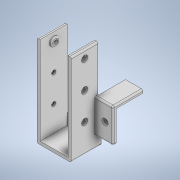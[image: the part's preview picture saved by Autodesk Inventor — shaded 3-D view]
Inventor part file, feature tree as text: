
AUTODESK INVENTOR PART (.ipt)
format: ipt  version: 2020 (Build 240168000, 168)  size: 286,208 bytes
history: native  units: in
note: dims shown in document units (in); Inventor stores cm internally (conversion verified against a paired STEP export)
features: extrude x12, sketch x12, fillet x3, mirror x2, pattern_linear x1
ambient origin geometry x8: Origin, YZ Plane, XZ Plane, XY Plane, X Axis, Y Axis, Z Axis, Center Point
bodies: Solid1 (feature_tree)
feature tree (30):
  extrude  "Extrusion1"  Depth=1.0in
  extrude  "Extrusion2"  Depth=0.1181in
  extrude  "Extrusion3"  Depth=3.2972in TaperAngle=0.0deg
  extrude  "Extrusion4"  Depth=0.1181in TaperAngle=0.0deg
  extrude  "Extrusion5"  Depth=0.0591in TaperAngle=0.0deg
  fillet  "Fillet1"  Radius=0.3346in
  pattern_linear  "Rectangular Pattern1"  Count1=3 Spacing1=-1.0236in
  mirror  "Mirror2"
  extrude  "Extrusion6"  Depth=1.2756in
  extrude  "Extrusion7"  Depth=0.6811in
  extrude  "Extrusion8"  Depth=0.2362in
  extrude  "Extrusion9"  Depth=0.0787in
  fillet  "Fillet2"  Radius=0.0787in
  extrude  "Extrusion11"  Depth=0.1181in TaperAngle=0.0deg
  extrude  "Extrusion14"  Depth=0.6496in
  mirror  "Mirror4"
  fillet  "Fillet5"  Radius=0.1181in
  extrude  "Extrusion15"  Depth=1.0in TaperAngle=0.0deg
  sketch  "Sketch1"  dims[d0=1.2756in d1=1.0in]
  sketch  "Sketch2"  dims[d2=0.1181in d3=0.0in d4=0.1181in]
  sketch  "Sketch3"  dims[d5=0.1181in d6=3.2972in d7=0.0in]
  sketch  "Sketch4"  dims[d8=0.1575in d9=0.1181in d10=0.0in]
  sketch  "Sketch5"  dims[d11=0.2362in d12=0.0591in d13=0.0in d14=0.3346in]
  sketch  "Sketch6"  dims[d15=0.0787in d16=0.0in]
  sketch  "Sketch7"  dims[d17=0.0472in d18=1.1811in d20=-1.0236in]
  sketch  "Sketch8"  dims[d21=0.1181in d22=1.2756in]
  sketch  "Sketch9"  dims[d23=0.6811in d24=0.0in d25=0.1575in]
  sketch  "Sketch11"  dims[d26=0.1181in d27=0.0in d28=0.2362in]
  sketch  "Sketch14"  dims[d29=0.0591in d30=0.0in d31=0.3346in d32=0.0787in d33=0.0in]
  sketch  "Sketch15"  dims[d34=0.0591in d38=0.1181in d39=0.0in d48=0.6496in d49=0.1181in d50=1.0in d51=0.0in d53=0.0591in d54=1.5748in d55=0.0in]
